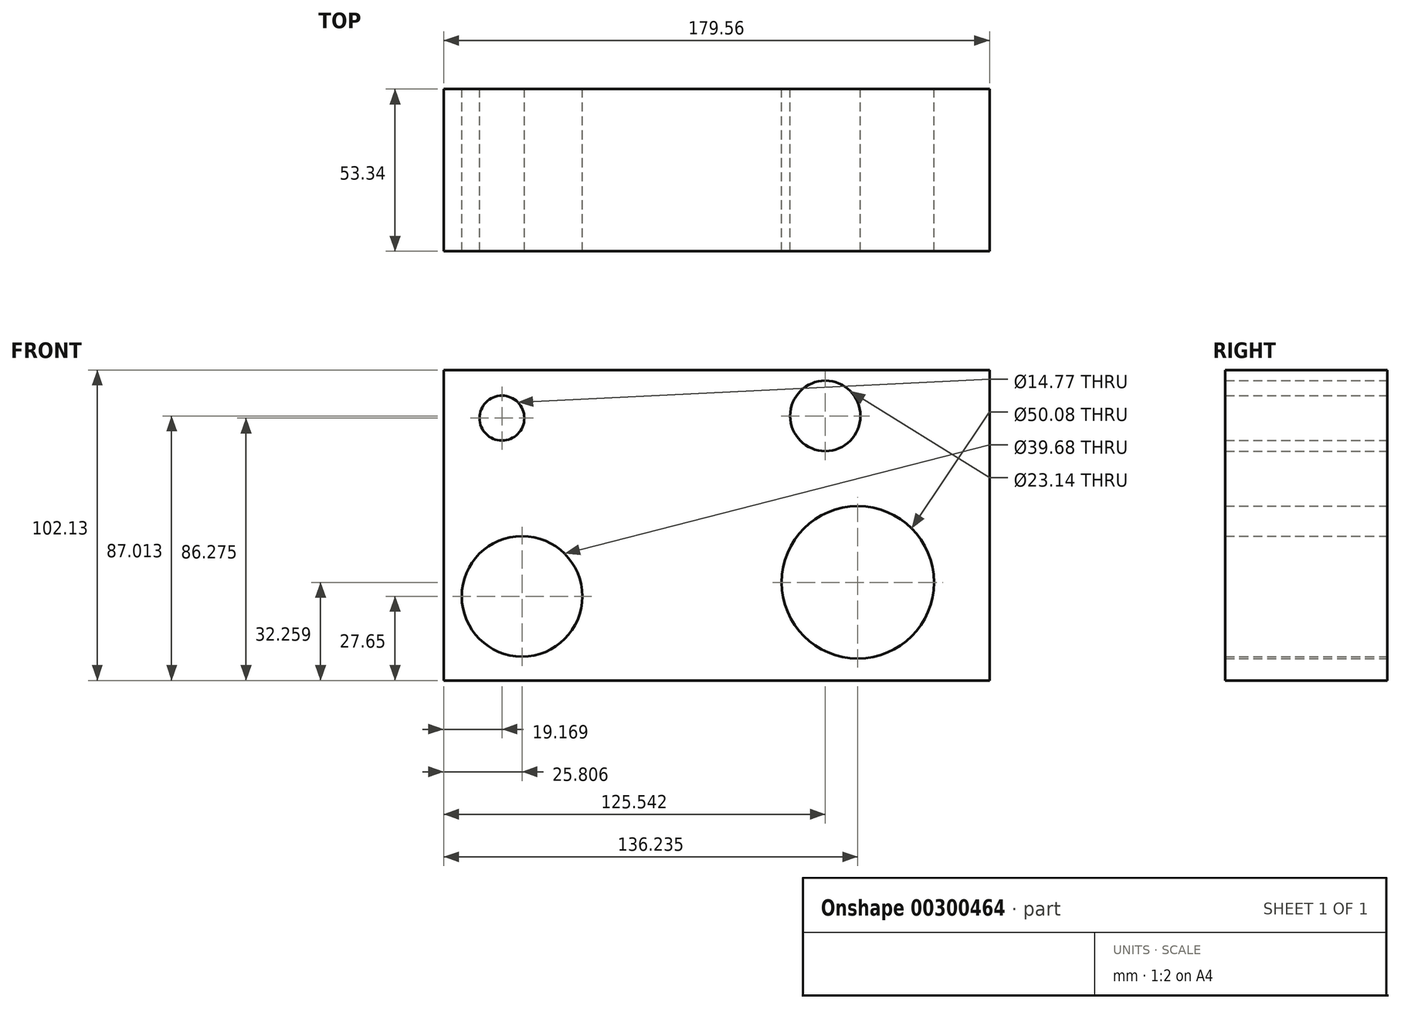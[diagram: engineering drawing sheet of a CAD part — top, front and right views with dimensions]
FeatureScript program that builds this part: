
annotation { "Feature Type Name" : "Feature", "Feature Type Description" : "" }
export const myFeature = defineFeature(function(context is Context, id is Id, definition is map)
    precondition{}
    {
        {
            var Q0;
            Q0=qCreatedBy(makeId("Front.planeOp"),FACE);
            var sketch = newSketch(context, id + "F0", { "sketchPlane" : qUnion([Q0])});
            skLineSegment(sketch, "E0.bottom", {"start": v(-93.28, 52.9) * mm, "end": v(86.28, 52.9) * mm});
            skLineSegment(sketch, "E0.top", {"start": v(-93.28, -49.22) * mm, "end": v(86.28, -49.22) * mm});
            skLineSegment(sketch, "E0.left", {"start": v(-93.28, 52.9) * mm, "end": v(-93.28, -49.22) * mm});
            skLineSegment(sketch, "E0.right", {"start": v(86.28, 52.9) * mm, "end": v(86.28, -49.22) * mm});
            skCircle(sketch, "E1", {"center": v(-74.11, 37.06) * mm, "radius": 7.38 * mm});
            skCircle(sketch, "E2", {"center": v(42.95, -16.96) * mm, "radius": 25.04 * mm});
            skCircle(sketch, "E3", {"center": v(-67.47, -21.57) * mm, "radius": 19.84 * mm});
            skCircle(sketch, "E4", {"center": v(32.26, 37.8) * mm, "radius": 11.57 * mm});
            skSolve(sketch);
        }
        {
            var Q0;
            Q0=makeQuery(id+"F0.imprint","IMPRINT",FACE,{"disambiguationData":[TD([[makeQuery(id+"F0.imprint","IMPRINT",EDGE,{"derivedFrom":sQuery(id+"F0.wireOp",EDGE,"E0.bottom")}),-1.0]])]});
            extrude(context, id + "F1", {"entities" : qUnion([Q0]), "depth" : 53.34 * mm});
        }
    });
